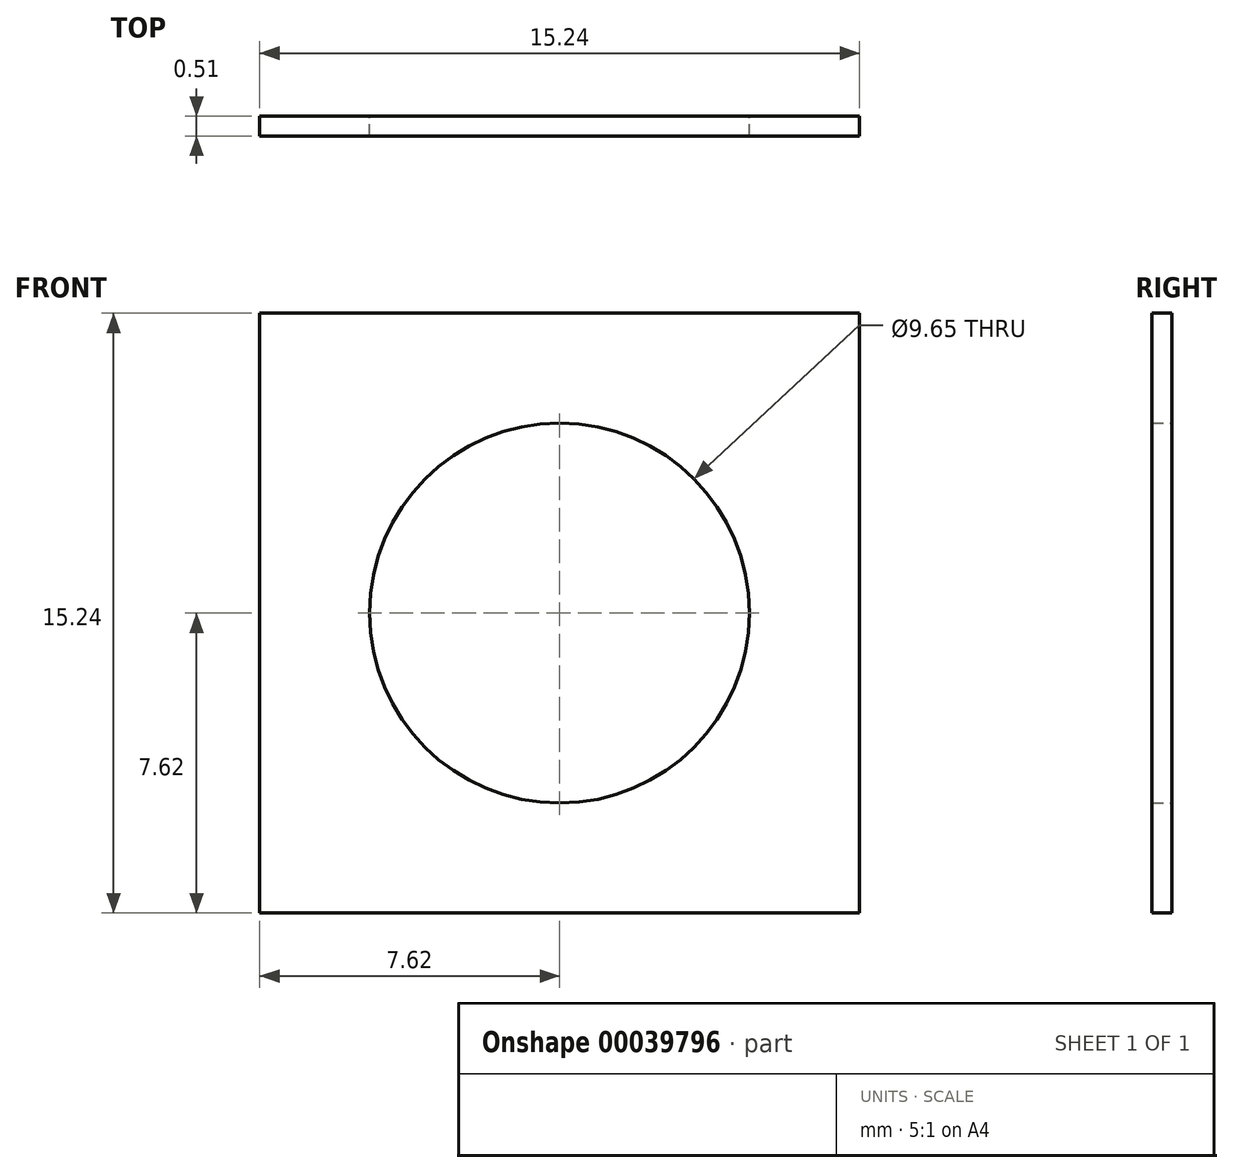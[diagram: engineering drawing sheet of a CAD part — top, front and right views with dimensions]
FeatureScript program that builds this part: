
annotation { "Feature Type Name" : "Feature", "Feature Type Description" : "" }
export const myFeature = defineFeature(function(context is Context, id is Id, definition is map)
    precondition{}
    {
        {
            var Q0;
            Q0=qCreatedBy(makeId("Front.planeOp"),FACE);
            var sketch = newSketch(context, id + "F0", { "sketchPlane" : qUnion([Q0])});
            skLineSegment(sketch, "E0.bottom", {"start": v(0, 0) * mm, "end": v(15.24, 0) * mm});
            skLineSegment(sketch, "E0.top", {"start": v(0, 15.24) * mm, "end": v(15.24, 15.24) * mm});
            skLineSegment(sketch, "E0.left", {"start": v(0, 0) * mm, "end": v(0, 15.24) * mm});
            skLineSegment(sketch, "E0.right", {"start": v(15.24, 0) * mm, "end": v(15.24, 15.24) * mm});
            skLineSegment(sketch, "E1", {"start": v(7.62, 15.24) * mm, "end": v(7.62, 0) * mm, "construction": true});
            skLineSegment(sketch, "E2", {"start": v(15.24, 7.62) * mm, "end": v(0, 7.62) * mm, "construction": true});
            skLineSegment(sketch, "E3", {"start": v(7.62, 7.62) * mm, "end": v(12.45, 7.62) * mm});
            skCircle(sketch, "E4", {"center": v(7.62, 7.62) * mm, "radius": 4.83 * mm});
            skSolve(sketch);
        }
        {
            var Q0;
            Q0 = qSketchRegion(id + "F0", true);
            extrude(context, id + "F1", {"entities" : qUnion([Q0]), "depth" : 0.5 * mm});
        }
    });
